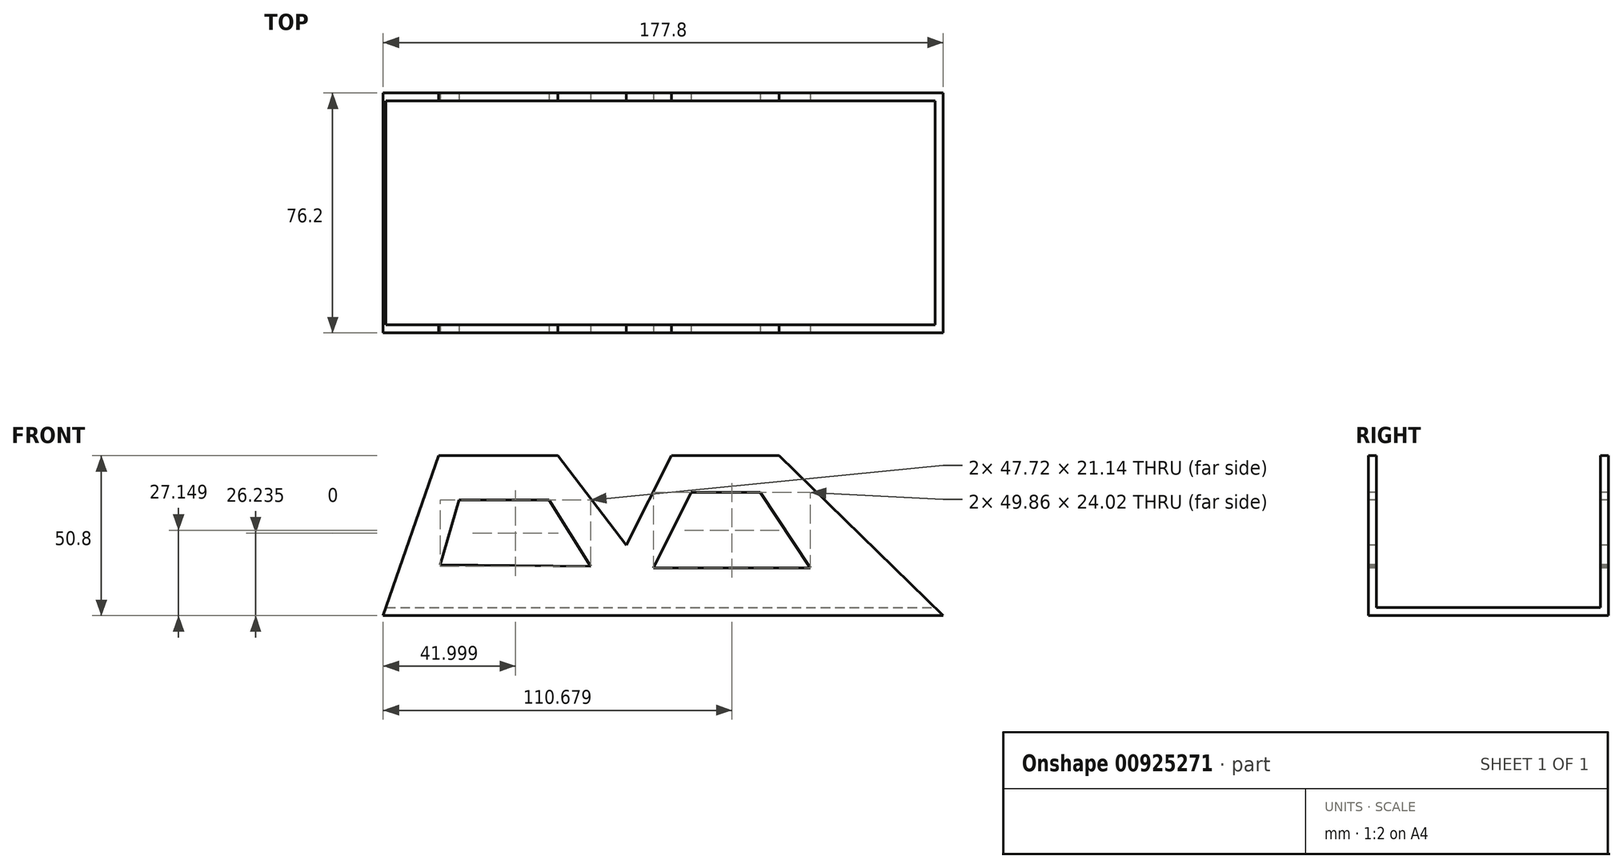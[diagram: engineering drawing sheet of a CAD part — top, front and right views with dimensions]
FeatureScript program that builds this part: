
annotation { "Feature Type Name" : "Feature", "Feature Type Description" : "" }
export const myFeature = defineFeature(function(context is Context, id is Id, definition is map)
    precondition{}
    {
        {
            var Q0;
            Q0=qCreatedBy(makeId("Top.planeOp"),FACE);
            var sketch = newSketch(context, id + "F0", { "sketchPlane" : qUnion([Q0])});
            skLineSegment(sketch, "E0.bottom", {"start": v(-65.86, 19.17) * mm, "end": v(111.94, 19.17) * mm});
            skLineSegment(sketch, "E0.top", {"start": v(-65.86, -57.03) * mm, "end": v(111.94, -57.03) * mm});
            skLineSegment(sketch, "E0.left", {"start": v(-65.86, 19.17) * mm, "end": v(-65.86, -57.03) * mm});
            skLineSegment(sketch, "E0.right", {"start": v(111.94, 19.17) * mm, "end": v(111.94, -57.03) * mm});
            skSolve(sketch);
        }
        {
            var Q0;
            Q0=makeQuery(id+"F0.imprint","IMPRINT",FACE,{"disambiguationData":[TD([[makeQuery(id+"F0.imprint","IMPRINT",EDGE,{"derivedFrom":sQuery(id+"F0.wireOp",EDGE,"E0.bottom")}),-1.0]])]});
            extrude(context, id + "F1", {"entities" : qUnion([Q0]), "depth" : 50.8 * mm, "offsetDistance" : 25.4 * mm});
        }
        {
            var Q0;
            Q0=makeQuery(id+"F1.opExtrude","CAP_FACE",FACE,{"disambiguationData":[OSD([sQuery(id+"F0.wireOp",EDGE,"E0.bottom"),sQuery(id+"F0.wireOp",EDGE,"E0.top"),sQuery(id+"F0.wireOp",EDGE,"E0.left"),sQuery(id+"F0.wireOp",EDGE,"E0.right")])],"isStart":false});
            var Q1;
            Q1=makeQuery(id+"F1.opExtrude","SWEPT_FACE",FACE,{"disambiguationData":[OSD([sQuery(id+"F0.wireOp",EDGE,"E0.left")])]});
            var Q2;
            Q2=makeQuery(id+"F1.opExtrude","SWEPT_FACE",FACE,{"disambiguationData":[OSD([sQuery(id+"F0.wireOp",EDGE,"E0.right")])]});
            shell(context, id + "F2", {"entities" : qUnion([Q0, Q1, Q2]), "thickness" : 2.54 * mm});
        }
        {
            var Q0;
            Q0=makeQuery(id+"F1.opExtrude","SWEPT_FACE",FACE,{"disambiguationData":[OSD([sQuery(id+"F0.wireOp",EDGE,"E0.top")])]});
            var sketch = newSketch(context, id + "F3", { "sketchPlane" : qUnion([Q0])});
            skLineSegment(sketch, "E1", {"start": v(-65.86, 0) * mm, "end": v(-48.24, 50.8) * mm});
            skLineSegment(sketch, "E2", {"start": v(-48.24, 50.8) * mm, "end": v(-10.4, 50.8) * mm});
            skLineSegment(sketch, "E3", {"start": v(-10.4, 50.8) * mm, "end": v(11.28, 22.45) * mm});
            skLineSegment(sketch, "E4", {"start": v(11.28, 22.45) * mm, "end": v(25.63, 50.8) * mm});
            skLineSegment(sketch, "E5", {"start": v(25.63, 50.8) * mm, "end": v(59.83, 50.8) * mm});
            skLineSegment(sketch, "E6", {"start": v(59.83, 50.8) * mm, "end": v(111.94, 0) * mm});
            skLineSegment(sketch, "E7", {"start": v(111.94, 0) * mm, "end": v(111.94, 69.44) * mm});
            skLineSegment(sketch, "E8", {"start": v(111.94, 69.44) * mm, "end": v(-74.45, 69.44) * mm});
            skLineSegment(sketch, "E9", {"start": v(-74.45, 69.44) * mm, "end": v(-65.86, 0) * mm});
            skSolve(sketch);
        }
        {
            var Q0;
            Q0 = qSketchRegion(id + "F3", true);
            extrude(context, id + "F4", {"entities" : qUnion([Q0]), "operationType" : NewBodyOperationType.REMOVE, "endBound" : BoundingType.THROUGH_ALL, "oppositeDirection" : true, "depth" : 25.4 * mm, "offsetDistance" : 25.4 * mm});
        }
        {
            var Q0;
            Q0=makeQuery(id+"F1.opExtrude","SWEPT_FACE",FACE,{"disambiguationData":[OSD([sQuery(id+"F0.wireOp",EDGE,"E0.top")])]});
            var sketch = newSketch(context, id + "F5", { "sketchPlane" : qUnion([Q0])});
            skLineSegment(sketch, "E10", {"start": v(-47.72, 16.18) * mm, "end": v(-41.72, 36.8) * mm});
            skLineSegment(sketch, "E11", {"start": v(-41.72, 36.8) * mm, "end": v(-13.26, 36.8) * mm});
            skLineSegment(sketch, "E12", {"start": v(-13.26, 36.8) * mm, "end": v(0, 15.66) * mm});
            skLineSegment(sketch, "E13", {"start": v(0, 15.66) * mm, "end": v(-47.72, 16.18) * mm});
            skSolve(sketch);
        }
        {
            var Q0;
            Q0 = qSketchRegion(id + "F5", true);
            extrude(context, id + "F6", {"entities" : qUnion([Q0]), "operationType" : NewBodyOperationType.REMOVE, "endBound" : BoundingType.THROUGH_ALL, "oppositeDirection" : true, "depth" : 25.4 * mm, "offsetDistance" : 25.4 * mm});
        }
        {
            var Q0;
            Q0=makeQuery(id+"F1.opExtrude","SWEPT_FACE",FACE,{"disambiguationData":[OSD([sQuery(id+"F0.wireOp",EDGE,"E0.top")])]});
            var sketch = newSketch(context, id + "F7", { "sketchPlane" : qUnion([Q0])});
            skLineSegment(sketch, "E14", {"start": v(19.89, 15.14) * mm, "end": v(31.9, 39.16) * mm});
            skLineSegment(sketch, "E15", {"start": v(31.9, 39.16) * mm, "end": v(53.83, 39.16) * mm});
            skLineSegment(sketch, "E16", {"start": v(53.83, 39.16) * mm, "end": v(69.75, 15.14) * mm});
            skLineSegment(sketch, "E17", {"start": v(19.89, 15.14) * mm, "end": v(69.75, 15.14) * mm});
            skSolve(sketch);
        }
        {
            var Q0;
            Q0 = qSketchRegion(id + "F7", true);
            extrude(context, id + "F8", {"entities" : qUnion([Q0]), "operationType" : NewBodyOperationType.REMOVE, "endBound" : BoundingType.THROUGH_ALL, "oppositeDirection" : true, "depth" : 25.4 * mm, "offsetDistance" : 25.4 * mm});
        }
    });
